# Revit family: Plymold-Essentials-Square_Metal_Top-Waste-Receptacle-
name_source: partatom
category: Furniture
units: mm (PartAtom-declared; Revit-internal decimal feet)

## family parameters
Always vertical = Yes
Cut with Voids When Loaded = No
OmniClass Number = 23.40.20.00
OmniClass Title = General Furniture and Specialties
Render Appearance Source = Family Geometry
Room Calculation Point = No
Shared = No
Work Plane-Based = No

## types (1)
- 80171
    Assembly Code = E2020200
    BACK MATERIAL = PLY - Natural Maple Vertical
    Brand = Receptacle
    CAP MATERIAL = PLY - Plastic Black
    CASTER MATERIAL = PLY - Metal_Galvanized
    Cost = 0 $
    DOOR MATERIAL = PLY - Natural Maple Vertical
    Default Elevation = 0"
    Depth = 24"
    Description = Square Tube Metal Top Waste Receptacle - 22 1/8"W x 24"D x 42 1/2"H
    FRAME MATERIAL = PLY - Starburst Silver Powdercoat
    Height = 42 1/2"
    Keynote = 12500
    LINER MATERIAL = PLY - Plastic Black
    Manufacturer = Plymold
    Model = 80171
    Product Documentation Link = https://plymold.com
    Revit Model Built By = https://www.servex-us.com
    SIDE MATERIAL = PLY - Natural Maple Vertical
    Sustainability = https://plymold.com
    TOP MATERIAL = PLY - Starburst Silver Powdercoat
    Type Comments = Casegoods
    URL = https://plymold.com
    WHEEL MATERIAL = PLY - Plastic Black
    Width = 22 1/8"

## geometry (parser evidence)
native form markers: Sweep x6
no freeform markers — native parametric forms only
